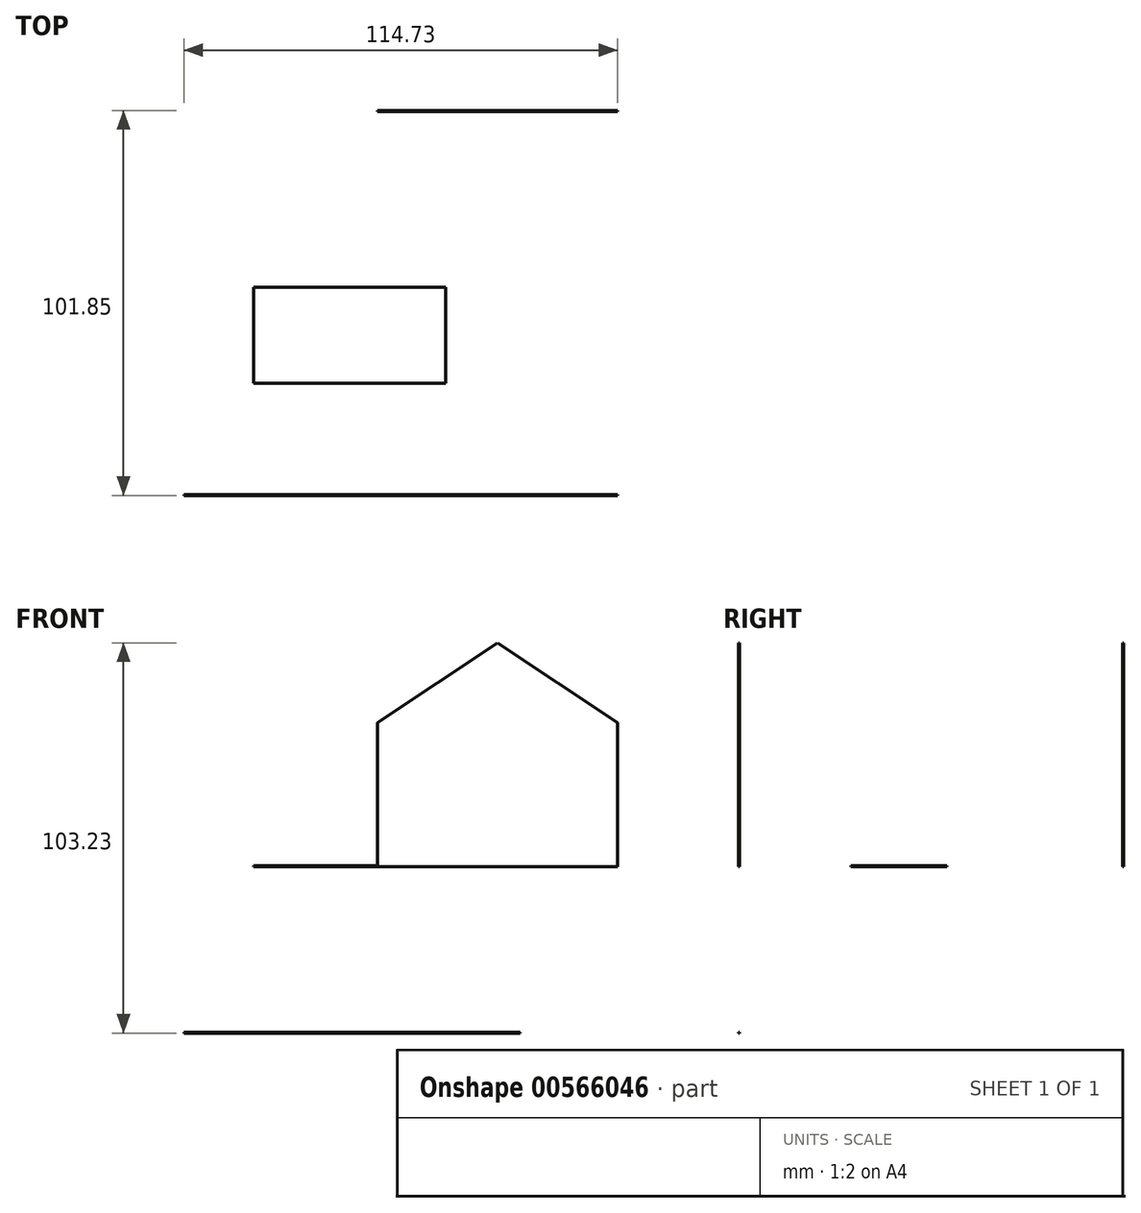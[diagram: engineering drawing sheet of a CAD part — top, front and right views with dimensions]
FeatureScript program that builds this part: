
annotation { "Feature Type Name" : "Feature", "Feature Type Description" : "" }
export const myFeature = defineFeature(function(context is Context, id is Id, definition is map)
    precondition{}
    {
        {
            var Q0;
            Q0=qCreatedBy(makeId("Front.planeOp"),FACE);
            var sketch = newSketch(context, id + "F0", { "sketchPlane" : qUnion([Q0])});
            skLineSegment(sketch, "E0.bottom", {"start": v(-28.01, 38.1) * mm, "end": v(35.49, 38.1) * mm});
            skLineSegment(sketch, "E0.top", {"start": v(-28.01, 0) * mm, "end": v(35.49, 0) * mm});
            skLineSegment(sketch, "E0.left", {"start": v(-28.01, 38.1) * mm, "end": v(-28.01, 0) * mm});
            skLineSegment(sketch, "E0.right", {"start": v(35.49, 38.1) * mm, "end": v(35.49, 0) * mm});
            skLineSegment(sketch, "E1", {"start": v(-28.01, 38.1) * mm, "end": v(3.74, 59.16) * mm});
            skPoint(sketch, "E1.endSnap0", {"position": v(3.74, 38.1) * mm});
            skLineSegment(sketch, "E2", {"start": v(3.74, 59.16) * mm, "end": v(35.49, 38.1) * mm});
            skSolve(sketch);
        }
        {
            var Q0;
            Q0=makeQuery(id+"F0.imprint","IMPRINT",FACE,{"disambiguationData":[TD([[makeQuery(id+"F0.imprint","IMPRINT",EDGE,{"derivedFrom":sQuery(id+"F0.wireOp",EDGE,"E0.bottom")}),-1.0]])]});
            cPlane(context, id + "F1", {"entities" : qUnion([Q0]), "cplaneType" : CPlaneType.OFFSET, "offset" : 101.6 * mm, "oppositeDirection" : true, "width" : 152.4 * mm, "height" : 152.4 * mm});
        }
        {
            var Q0;
            Q0=qCreatedBy(id+"F1.planeOp",FACE);
            var sketch = newSketch(context, id + "F2", { "sketchPlane" : qUnion([Q0])});
            skLineSegment(sketch, "E3.bottom", {"start": v(35.49, 38.1) * mm, "end": v(-28.01, 38.1) * mm});
            skLineSegment(sketch, "E3.top", {"start": v(35.49, 0) * mm, "end": v(-28.01, 0) * mm});
            skLineSegment(sketch, "E3.left", {"start": v(35.49, 38.1) * mm, "end": v(35.49, 0) * mm});
            skLineSegment(sketch, "E3.right", {"start": v(-28.01, 38.1) * mm, "end": v(-28.01, 0) * mm});
            skLineSegment(sketch, "E4", {"start": v(35.49, 38.1) * mm, "end": v(3.74, 59.16) * mm});
            skPoint(sketch, "E4.endSnap0", {"position": v(3.74, 38.1) * mm});
            skLineSegment(sketch, "E5", {"start": v(3.74, 59.16) * mm, "end": v(-28.01, 38.1) * mm});
            skSolve(sketch);
        }
        {
            var Q0;
            Q0 = qSketchRegion(id + "F0", true);
            extrude(context, id + "F3", {"entities" : qUnion([Q0]), "depth" : 0.25 * mm, "offsetDistance" : 25.4 * mm});
        }
        {
            var Q0;
            Q0 = qSketchRegion(id + "F2", true);
            extrude(context, id + "F4", {"entities" : qUnion([Q0]), "depth" : 0.25 * mm, "offsetDistance" : 25.4 * mm});
        }
        {
            var Q0;
            Q0=qCreatedBy(makeId("Front.planeOp"),FACE);
            var sketch = newSketch(context, id + "F5", { "sketchPlane" : qUnion([Q0])});
            skLineSegment(sketch, "E6.bottom", {"start": v(-79.24, -44.07) * mm, "end": v(9.66, -44.07) * mm});
            skLineSegment(sketch, "E6.top", {"start": v(-79.24, -43.82) * mm, "end": v(9.66, -43.82) * mm});
            skLineSegment(sketch, "E6.left", {"start": v(-79.24, -44.07) * mm, "end": v(-79.24, -43.82) * mm});
            skLineSegment(sketch, "E6.right", {"start": v(9.66, -44.07) * mm, "end": v(9.66, -43.82) * mm});
            skSolve(sketch);
        }
        {
            var Q0;
            Q0 = qSketchRegion(id + "F5", true);
            extrude(context, id + "F6", {"entities" : qUnion([Q0]), "depth" : 0.25 * mm, "offsetDistance" : 25.4 * mm});
        }
        {
            var Q0;
            Q0=makeQuery(id+"F5.imprint","IMPRINT",FACE,{"disambiguationData":[TD([[makeQuery(id+"F5.imprint","IMPRINT",EDGE,{"derivedFrom":sQuery(id+"F5.wireOp",EDGE,"E6.bottom")}),1.0]])]});
            extrude(context, id + "F7", {"entities" : qUnion([Q0]), "operationType" : NewBodyOperationType.ADD, "depth" : 0.25 * mm, "offsetDistance" : 25.4 * mm});
        }
        {
            var Q0;
            Q0=qCreatedBy(makeId("Top.planeOp"),FACE);
            var sketch = newSketch(context, id + "F8", { "sketchPlane" : qUnion([Q0])});
            skLineSegment(sketch, "E7.bottom", {"start": v(-60.82, 54.83) * mm, "end": v(-10.02, 54.83) * mm});
            skLineSegment(sketch, "E7.top", {"start": v(-60.82, 29.43) * mm, "end": v(-10.02, 29.43) * mm});
            skLineSegment(sketch, "E7.left", {"start": v(-60.82, 54.83) * mm, "end": v(-60.82, 29.43) * mm});
            skLineSegment(sketch, "E7.right", {"start": v(-10.02, 54.83) * mm, "end": v(-10.02, 29.43) * mm});
            skSolve(sketch);
        }
        {
            var Q0;
            Q0 = qSketchRegion(id + "F8", true);
            extrude(context, id + "F9", {"entities" : qUnion([Q0]), "depth" : 0.25 * mm, "offsetDistance" : 25.4 * mm});
        }
    });
